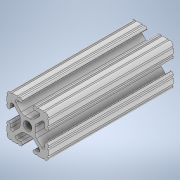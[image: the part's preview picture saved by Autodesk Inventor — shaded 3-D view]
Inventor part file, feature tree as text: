
AUTODESK INVENTOR PART (.ipt)
format: ipt  version: 2020 (Build 240168000, 168)  size: 236,032 bytes
history: native  units: in
note: dims shown in document units (in); Inventor stores cm internally (conversion verified against a paired STEP export)
features: extrude x1, sketch x1
ambient origin geometry x8: Origin, YZ Plane, XZ Plane, XY Plane, X Axis, Y Axis, Z Axis, Center Point
bodies: Solid1 (feature_tree)
feature tree (2):
  extrude  "Extrusion1"  [1 undecoded]
  sketch  "Sketch1"  dims[d0=3.0in d1=0.0in]
note: 1 required parameter value undecoded (feature->parameter linkage not recoverable at this tier; creation-order binding heuristic only, values carry confidence <= 0.55)
